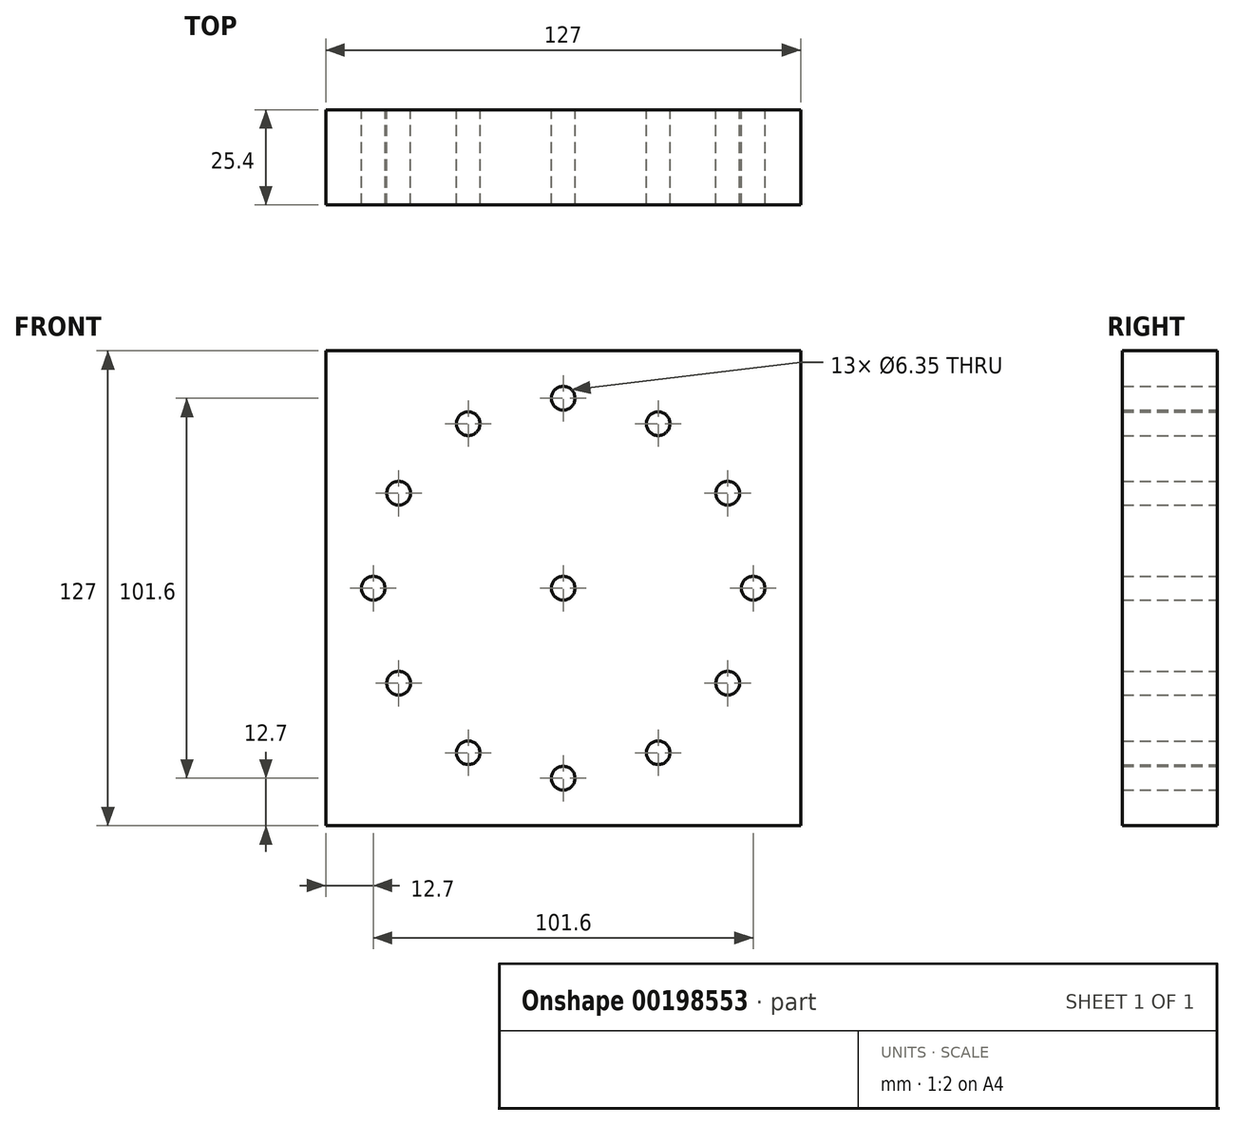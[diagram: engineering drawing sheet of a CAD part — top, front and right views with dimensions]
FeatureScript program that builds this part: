
annotation { "Feature Type Name" : "Feature", "Feature Type Description" : "" }
export const myFeature = defineFeature(function(context is Context, id is Id, definition is map)
    precondition{}
    {
        {
            var Q0;
            Q0=qCreatedBy(makeId("Front.planeOp"),FACE);
            var sketch = newSketch(context, id + "F0", { "sketchPlane" : qUnion([Q0])});
            skLineSegment(sketch, "E0.bottom", {"start": v(63.5, 63.5) * mm, "end": v(-63.5, 63.5) * mm});
            skLineSegment(sketch, "E0.top", {"start": v(63.5, -63.5) * mm, "end": v(-63.5, -63.5) * mm});
            skLineSegment(sketch, "E0.left", {"start": v(63.5, 63.5) * mm, "end": v(63.5, -63.5) * mm});
            skLineSegment(sketch, "E0.right", {"start": v(-63.5, 63.5) * mm, "end": v(-63.5, -63.5) * mm});
            skPoint(sketch, "E0.middle", {"position": v(0, 0) * mm});
            skCircle(sketch, "E1", {"center": v(0, 0) * mm, "radius": 50.8 * mm, "construction": true});
            skCircle(sketch, "E2", {"center": v(0, 0) * mm, "radius": 3.18 * mm});
            skCircle(sketch, "E3", {"center": v(0, 50.8) * mm, "radius": 3.18 * mm});
            skPoint(sketch, "E3.centerSnap0", {"position": v(0, 63.5) * mm});
            skCircle(sketch, "E4.1.0", {"center": v(-25.4, 44) * mm, "radius": 3.18 * mm});
            skCircle(sketch, "E4.2.0", {"center": v(-44, 25.4) * mm, "radius": 3.18 * mm});
            skCircle(sketch, "E4.3.0", {"center": v(-50.8, 0) * mm, "radius": 3.18 * mm});
            skCircle(sketch, "E4.4.0", {"center": v(-44, -25.4) * mm, "radius": 3.18 * mm});
            skCircle(sketch, "E4.5.0", {"center": v(-25.4, -44) * mm, "radius": 3.18 * mm});
            skCircle(sketch, "E4.6.0", {"center": v(0, -50.8) * mm, "radius": 3.18 * mm});
            skCircle(sketch, "E4.7.0", {"center": v(25.4, -44) * mm, "radius": 3.18 * mm});
            skCircle(sketch, "E4.8.0", {"center": v(44, -25.4) * mm, "radius": 3.18 * mm});
            skCircle(sketch, "E4.9.0", {"center": v(50.8, 0) * mm, "radius": 3.18 * mm});
            skCircle(sketch, "E4.10.0", {"center": v(44, 25.4) * mm, "radius": 3.18 * mm});
            skCircle(sketch, "E4.11.0", {"center": v(25.4, 44) * mm, "radius": 3.18 * mm});
            skSolve(sketch);
        }
        {
            var Q0;
            Q0 = qSketchRegion(id + "F0", true);
            extrude(context, id + "F1", {"entities" : qUnion([Q0]), "depth" : 25.4 * mm, "offsetDistance" : 25.4 * mm});
        }
    });
